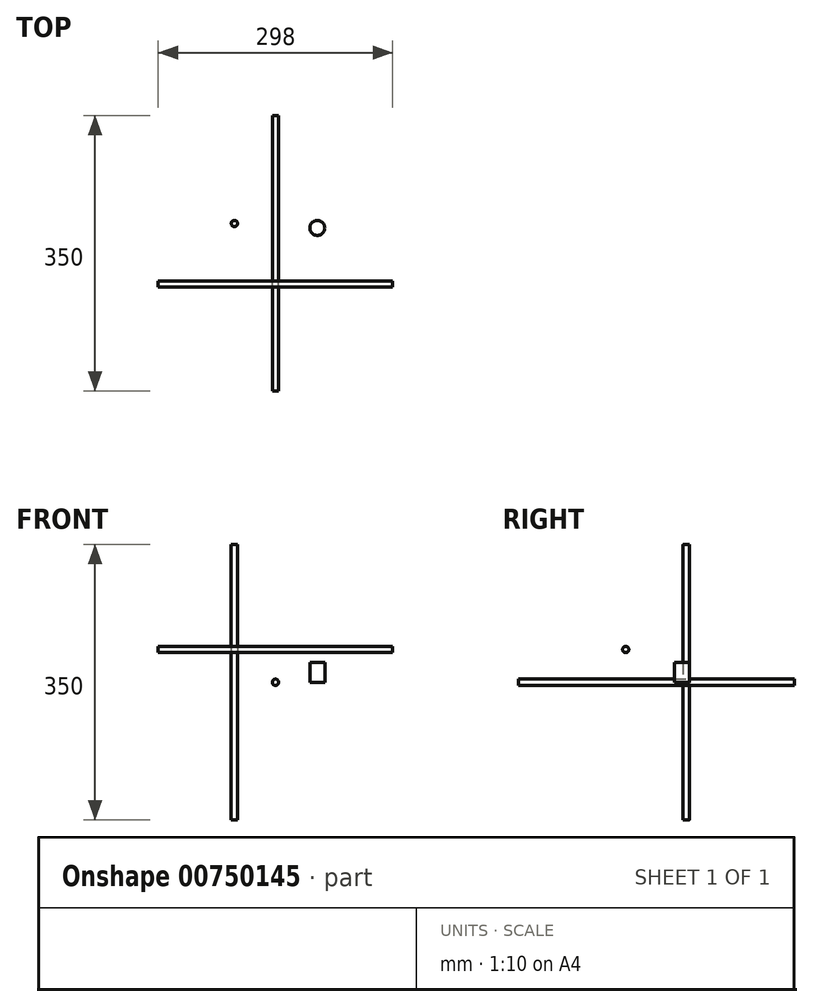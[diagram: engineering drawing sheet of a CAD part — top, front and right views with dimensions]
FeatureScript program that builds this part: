
annotation { "Feature Type Name" : "Feature", "Feature Type Description" : "" }
export const myFeature = defineFeature(function(context is Context, id is Id, definition is map)
    precondition{}
    {
        {
            var Q0;
            Q0=qCreatedBy(makeId("Front.planeOp"),FACE);
            var sketch = newSketch(context, id + "F0", { "sketchPlane" : qUnion([Q0])});
            skCircle(sketch, "E0", {"center": v(0, 0) * mm, "radius": 4 * mm});
            skSolve(sketch);
        }
        {
            var Q0;
            Q0=makeQuery(id+"F0.imprint","IMPRINT",FACE,{"disambiguationData":[TD([[makeQuery(id+"F0.imprint","IMPRINT",EDGE,{"derivedFrom":sQuery(id+"F0.wireOp",EDGE,"E0")}),1.0]])]});
            extrude(context, id + "F1", {"entities" : qUnion([Q0]), "depth" : 350 * mm, "flatOperationType" : FlatOperationType.REMOVE, "offsetDistance" : 25 * mm, "domain" : OperationDomain.MODEL, "symmetric" : true});
        }
        {
            var Q0;
            Q0=qCreatedBy(makeId("Top.planeOp"),FACE);
            var sketch = newSketch(context, id + "F2", { "sketchPlane" : qUnion([Q0])});
            skCircle(sketch, "E1", {"center": v(-52.16, 37.8) * mm, "radius": 4 * mm});
            skSolve(sketch);
        }
        {
            var Q0;
            Q0=makeQuery(id+"F2.imprint","IMPRINT",FACE,{"disambiguationData":[TD([[makeQuery(id+"F2.imprint","IMPRINT",EDGE,{"derivedFrom":sQuery(id+"F2.wireOp",EDGE,"E1")}),1.0]])]});
            extrude(context, id + "F3", {"entities" : qUnion([Q0]), "depth" : 350 * mm, "flatOperationType" : FlatOperationType.REMOVE, "offsetDistance" : 25 * mm, "domain" : OperationDomain.MODEL, "symmetric" : true});
        }
        {
            var Q0;
            Q0=qCreatedBy(makeId("Right.planeOp"),FACE);
            var sketch = newSketch(context, id + "F4", { "sketchPlane" : qUnion([Q0])});
            skCircle(sketch, "E2", {"center": v(-39.06, 41.64) * mm, "radius": 4 * mm});
            skSolve(sketch);
        }
        {
            var Q0;
            Q0=makeQuery(id+"F4.imprint","IMPRINT",FACE,{"disambiguationData":[TD([[makeQuery(id+"F4.imprint","IMPRINT",EDGE,{"derivedFrom":sQuery(id+"F4.wireOp",EDGE,"E2")}),1.0]])]});
            extrude(context, id + "F5", {"entities" : qUnion([Q0]), "depth" : 298 * mm, "offsetDistance" : 25 * mm, "symmetric" : true});
        }
        {
            var Q0;
            Q0=qCreatedBy(makeId("Top.planeOp"),FACE);
            var sketch = newSketch(context, id + "F6", { "sketchPlane" : qUnion([Q0])});
            skCircle(sketch, "E3", {"center": v(53.2, 32.14) * mm, "radius": 9.5 * mm});
            skSolve(sketch);
        }
        {
            var Q0;
            Q0=qSketchRegion(id+"F6",true);
            extrude(context, id + "F7", {"entities" : qUnion([Q0]), "depth" : 25 * mm, "offsetDistance" : 25 * mm});
        }
    });
